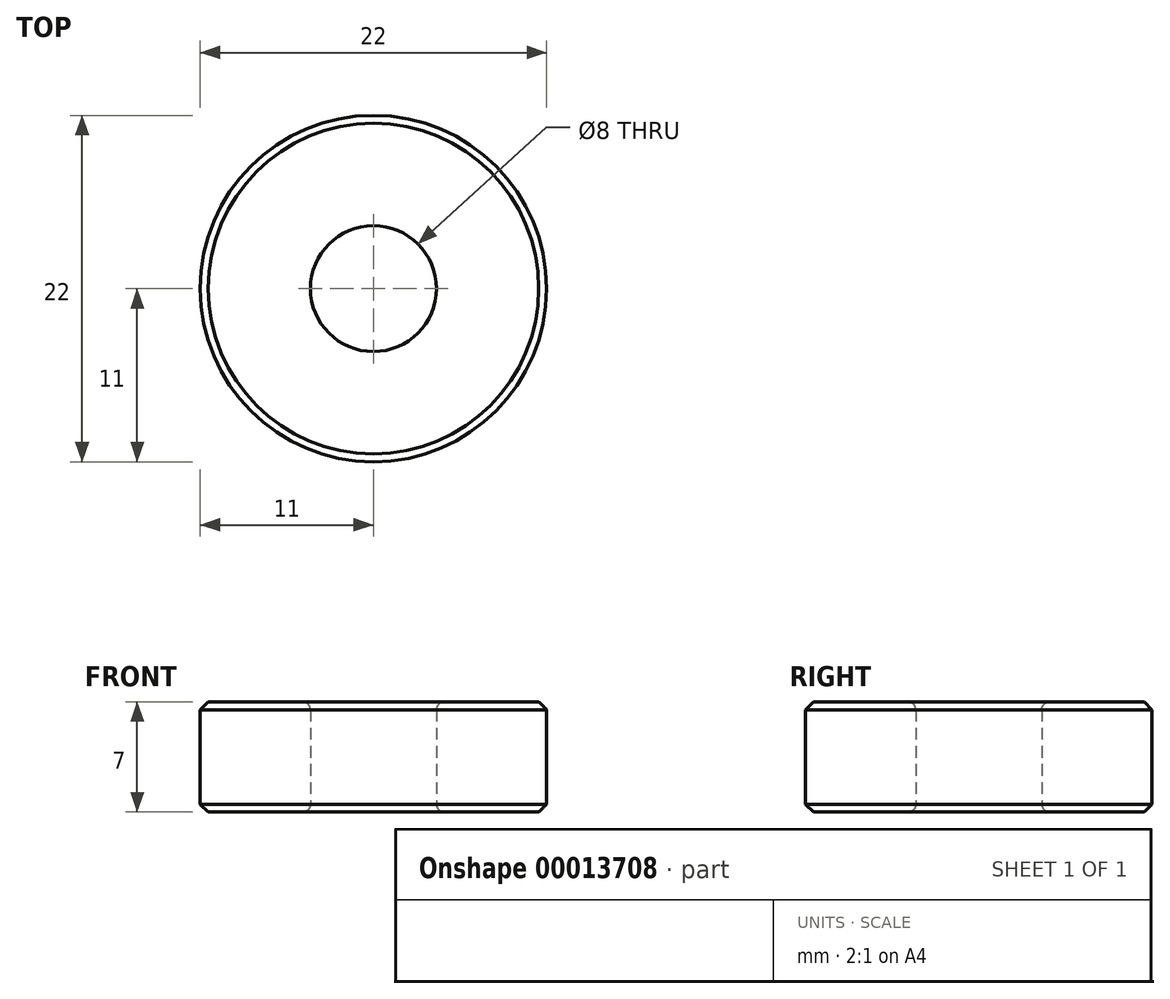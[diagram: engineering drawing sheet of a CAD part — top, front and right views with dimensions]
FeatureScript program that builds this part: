
annotation { "Feature Type Name" : "Feature", "Feature Type Description" : "" }
export const myFeature = defineFeature(function(context is Context, id is Id, definition is map)
    precondition{}
    {
        {
            var Q0;
            Q0=qCreatedBy(makeId("Top.planeOp"),FACE);
            var sketch = newSketch(context, id + "F0", { "sketchPlane" : qUnion([Q0])});
            skCircle(sketch, "E0", {"center": v(0, 0) * mm, "radius": 11 * mm});
            skCircle(sketch, "E1", {"center": v(0, 0) * mm, "radius": 4 * mm});
            skSolve(sketch);
        }
        {
            var Q0;
            Q0=makeQuery(id+"F0.imprint","IMPRINT",FACE,{"disambiguationData":[TD([[makeQuery(id+"F0.imprint","IMPRINT",EDGE,{"derivedFrom":sQuery(id+"F0.wireOp",EDGE,"E0")}),1.0]])]});
            extrude(context, id + "F1", {"entities" : qUnion([Q0]), "depth" : 7 * mm});
        }
        {
            var Q0;
            Q0=makeQuery(id+"F1.opExtrude","CAP_EDGE",EDGE,{"disambiguationData":[OSD([sQuery(id+"F0.wireOp",EDGE,"E0")])],"isStart":false});
            var Q1;
            Q1=makeQuery(id+"F1.opExtrude","CAP_EDGE",EDGE,{"disambiguationData":[OSD([sQuery(id+"F0.wireOp",EDGE,"E0")])],"isStart":true});
            chamfer(context, id + "F2", {"entities" : qUnion([Q0, Q1]), "width" : 0.5 * mm, "tangentPropagation" : true});
        }
        {
            var Q0;
            Q0=makeQuery(id+"F1.opExtrude","SWEPT_FACE",FACE,{"disambiguationData":[OSD([sQuery(id+"F0.wireOp",EDGE,"E1")])]});
            fillet(context, id + "F3", {"entities" : qUnion([Q0]), "radius" : 0.5 * mm, "tangentPropagation" : true, "allowEdgeOverflow" : false});
        }
    });
